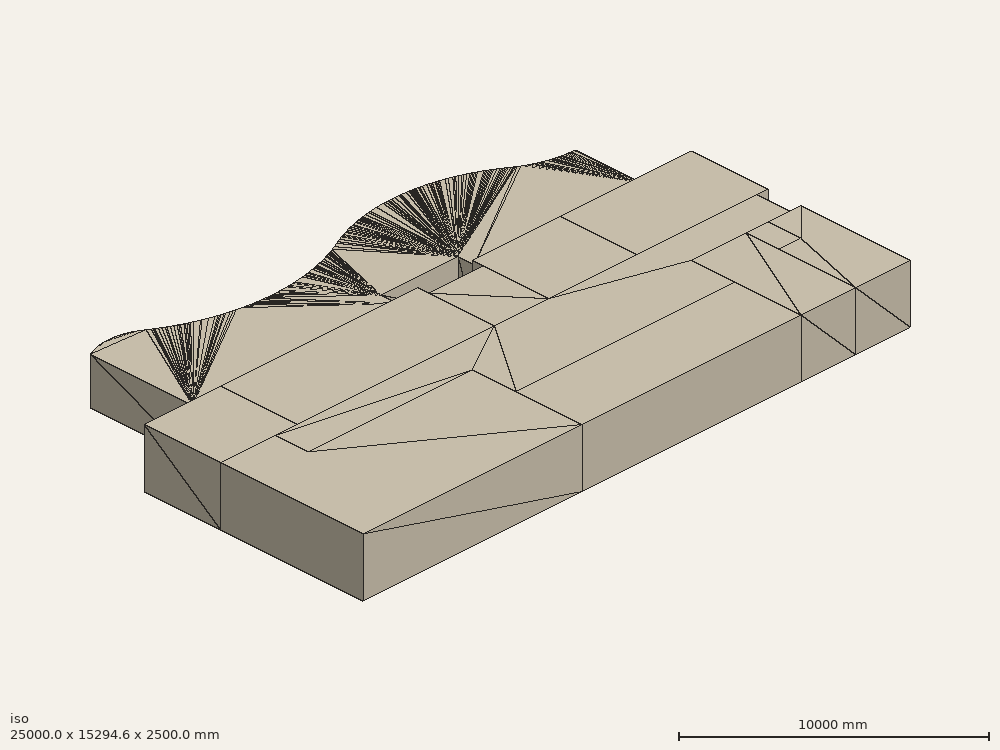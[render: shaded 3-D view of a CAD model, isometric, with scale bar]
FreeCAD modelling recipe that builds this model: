
FCSTD DOCUMENT  (FreeCAD 0.19R16466 (Git))
Label: Rooms_07
License: All rights reserved
LicenseURL: http://en.wikipedia.org/wiki/All_rights_reserved
objects: Part::FeaturePython×23, Part::Part2DObjectPython×10, App::GeometryPython×2, Sketcher::SketchObject×1
note: 36 computed .brp shape members not serialized (recipe doc carries the construction recipe); baked Part::Feature solids carry a one-line shape summary decoded from their .brp

FEATURE [Part::Part2DObjectPython] Wire  # Draft 2D object (typed FeaturePython)
  ChamferSize = 0
  Closed = true
  End = (0,6500,0)
  FilletRadius = 0
  Length = 33000
  MakeFace = true
  Points = (6) [(0,0,0),(10000,0,0),(10000,5000,0),(2500,5000,0),(2500,6500,0),(0,6500,0)]
  Start = (0,0,0)
  Subdivisions = 0
FEATURE [Part::Part2DObjectPython] Rectangle  # Draft 2D object (typed FeaturePython)
  ChamferSize = 0
  Columns = 1
  FilletRadius = 0
  Height = 3000
  Length = 10000
  MakeFace = true
  Placement = pos=(10000,0,0) rot=(0,0,1;0rad)
  Rows = 1
FEATURE [Part::Part2DObjectPython] Rectangle001  # Draft 2D object (typed FeaturePython)
  ChamferSize = 0
  Columns = 1
  FilletRadius = 0
  Height = 5000
  Length = 2500
  MakeFace = true
  Placement = pos=(20000,0,0) rot=(0,0,1;0rad)
  Rows = 1
FEATURE [Part::Part2DObjectPython] Wire001  # Draft 2D object (typed FeaturePython)
  ChamferSize = 0
  Closed = true
  End = (22500,3500,0)
  FilletRadius = 0
  Length = 15000
  MakeFace = true
  Points = (6) [(22500,0,0),(25000,0,0),(25000,5000,0),(23500,5000,0),(23500,3500,0),(22500,3500,0)]
  Start = (22500,0,0)
  Subdivisions = 0
FEATURE [Part::Part2DObjectPython] Rectangle002  # Draft 2D object (typed FeaturePython)
  ChamferSize = 0
  Columns = 1
  FilletRadius = 0
  Height = 1500
  Length = 1000
  MakeFace = true
  Placement = pos=(22500,3500,0) rot=(0,0,1;0rad)
  Rows = 1
FEATURE [Part::Part2DObjectPython] Rectangle003  # Draft 2D object (typed FeaturePython)
  ChamferSize = 0
  Columns = 1
  FilletRadius = 0
  Height = 3500
  Length = 3500
  MakeFace = true
  Placement = pos=(0,6500,0) rot=(0,0,1;0rad)
  Rows = 1
FEATURE [Part::Part2DObjectPython] Rectangle004  # Draft 2D object (typed FeaturePython)
  ChamferSize = 0
  Columns = 1
  FilletRadius = 0
  Height = 3500
  Length = 9000
  MakeFace = true
  Placement = pos=(3500,6500,0) rot=(0,0,1;0rad)
  Rows = 1
FEATURE [Part::Part2DObjectPython] Rectangle005  # Draft 2D object (typed FeaturePython)
  ChamferSize = 0
  Columns = 1
  FilletRadius = 0
  Height = 3500
  Length = 4000
  MakeFace = true
  Placement = pos=(15000,6500,0) rot=(0,0,1;0rad)
  Rows = 1
FEATURE [Part::Part2DObjectPython] Rectangle006  # Draft 2D object (typed FeaturePython)
  ChamferSize = 0
  Columns = 1
  FilletRadius = 0
  Height = 3500
  Length = 6000
  MakeFace = true
  Placement = pos=(19000,6500,0) rot=(0,0,1;0rad)
  Rows = 1
FEATURE [Part::Part2DObjectPython] Wire002  # Draft 2D object (typed FeaturePython)
  ChamferSize = 0
  Closed = true
  End = (10000,5000,0)
  FilletRadius = 0
  Length = 57000
  MakeFace = true
  Points = (12) [(2500,5000,0),(2500,6500,0),(12500,6500,0),(12500,9500,0),(15000,9500,0),(15000,6500,0),(24500,6500,0),(24500,5000,0),(20000,5000,0),(20000,3000,0),(10000,3000,0),(10000,5000,0)]
  Start = (2500,5000,0)
  Subdivisions = 0
FEATURE [Part::FeaturePython] Structure001  # Arch/BIM 0 (typed FeaturePython)
  Base = -> Rectangle002
  FaceMaker = 0
  Height = 2500
  HorizontalArea = 1.5e+06
  IfcData = attributes={"PredefinedType": {"name": "PredefinedType", "type": "IfcBeamTypeEnum", "is_enum": true, "enum_values": ["BEAM", "JOIST... (+96 chars omitted)
  IfcType = 0
  Length = 0
  MoveBase = false
  MoveWithHost = true
  Nodes = (2) [(23000,4250,0),(23000,4250,2500)]
  NodesOffset = 0
  Normal = (0,0,1)
  PerimeterLength = 5000
  PredefinedType = 0
  VerticalArea = 12500000
  Width = 200
FEATURE [Part::FeaturePython] Structure002  # Arch/BIM 0 (typed FeaturePython)
  Base = -> Rectangle001
  FaceMaker = 0
  Height = 2500
  HorizontalArea = 12500000
  IfcData = attributes={"PredefinedType": {"name": "PredefinedType", "type": "IfcBeamTypeEnum", "is_enum": true, "enum_values": ["BEAM", "JOIST... (+96 chars omitted)
  IfcType = 0
  Length = 0
  MoveBase = false
  MoveWithHost = true
  Nodes = (2) [(21250,2500,0),(21250,2500,2500)]
  NodesOffset = 0
  Normal = (0,0,1)
  PerimeterLength = 15000
  PredefinedType = 0
  VerticalArea = 37500000
  Width = 200
FEATURE [Part::FeaturePython] Structure003  # Arch/BIM 0 (typed FeaturePython)
  Base = -> Rectangle
  FaceMaker = 0
  Height = 2500
  HorizontalArea = 30000000
  IfcData = attributes={"PredefinedType": {"name": "PredefinedType", "type": "IfcBeamTypeEnum", "is_enum": true, "enum_values": ["BEAM", "JOIST... (+96 chars omitted)
  IfcType = 0
  Length = 0
  MoveBase = false
  MoveWithHost = true
  Nodes = (2) [(15000,1500,0),(15000,1500,2500)]
  NodesOffset = 0
  Normal = (0,0,1)
  PerimeterLength = 26000
  PredefinedType = 0
  VerticalArea = 65000000
  Width = 200
FEATURE [Part::FeaturePython] Structure004  # Arch/BIM 0 (typed FeaturePython)
  Base = -> Wire001
  FaceMaker = 0
  Height = 2500
  HorizontalArea = 11000000
  IfcData = attributes={"PredefinedType": {"name": "PredefinedType", "type": "IfcBeamTypeEnum", "is_enum": true, "enum_values": ["BEAM", "JOIST... (+96 chars omitted)
  IfcType = 0
  Length = 0
  MoveBase = false
  MoveWithHost = true
  Nodes = (2) [(23852.3,2261.36,0),(23852.3,2261.36,2500)]
  NodesOffset = 0
  Normal = (0,0,1)
  PerimeterLength = 15000
  PredefinedType = 0
  VerticalArea = 37500000
  Width = 200
FEATURE [Part::FeaturePython] Structure005  # Arch/BIM 0 (typed FeaturePython)
  Base = -> Rectangle005
  FaceMaker = 0
  Height = 2500
  HorizontalArea = 1.4e+07
  IfcData = attributes={"PredefinedType": {"name": "PredefinedType", "type": "IfcBeamTypeEnum", "is_enum": true, "enum_values": ["BEAM", "JOIST... (+96 chars omitted)
  IfcType = 0
  Length = 0
  MoveBase = false
  MoveWithHost = true
  Nodes = (2) [(17000,8250,0),(17000,8250,2500)]
  NodesOffset = 0
  Normal = (0,0,1)
  PerimeterLength = 15000
  PredefinedType = 0
  VerticalArea = 3.75e+07
  Width = 200
FEATURE [Part::FeaturePython] Structure006  # Arch/BIM 0 (typed FeaturePython)
  Base = -> Rectangle004
  FaceMaker = 0
  Height = 2500
  HorizontalArea = 31500000
  IfcData = attributes={"PredefinedType": {"name": "PredefinedType", "type": "IfcBeamTypeEnum", "is_enum": true, "enum_values": ["BEAM", "JOIST... (+96 chars omitted)
  IfcType = 0
  Length = 0
  MoveBase = false
  MoveWithHost = true
  Nodes = (2) [(8000,8250,0),(8000,8250,2500)]
  NodesOffset = 0
  Normal = (0,0,1)
  PerimeterLength = 25000
  PredefinedType = 0
  VerticalArea = 62500000
  Width = 200
FEATURE [Part::FeaturePython] Structure007  # Arch/BIM 0 (typed FeaturePython)
  Base = -> Rectangle003
  FaceMaker = 0
  Height = 2500
  HorizontalArea = 1.225e+07
  IfcData = attributes={"PredefinedType": {"name": "PredefinedType", "type": "IfcBeamTypeEnum", "is_enum": true, "enum_values": ["BEAM", "JOIST... (+96 chars omitted)
  IfcType = 0
  Length = 0
  MoveBase = false
  MoveWithHost = true
  Nodes = (2) [(1750,8250,0),(1750,8250,2500)]
  NodesOffset = 0
  Normal = (0,0,1)
  PerimeterLength = 14000
  PredefinedType = 0
  VerticalArea = 3.5e+07
  Width = 200
FEATURE [Part::FeaturePython] Structure008  # Arch/BIM 0 (typed FeaturePython)
  Base = -> Rectangle006
  FaceMaker = 0
  Height = 2500
  HorizontalArea = 21000000
  IfcData = attributes={"PredefinedType": {"name": "PredefinedType", "type": "IfcBeamTypeEnum", "is_enum": true, "enum_values": ["BEAM", "JOIST... (+96 chars omitted)
  IfcType = 0
  Length = 0
  MoveBase = false
  MoveWithHost = true
  Nodes = (2) [(22000,8250,0),(22000,8250,2500)]
  NodesOffset = 0
  Normal = (0,0,1)
  PerimeterLength = 19000
  PredefinedType = 0
  VerticalArea = 47500000
  Width = 200
FEATURE [Part::FeaturePython] Structure009  # Arch/BIM 0 (typed FeaturePython)
  Base = -> Wire002
  FaceMaker = 0
  Height = 2500
  HorizontalArea = 60500000
  IfcData = attributes={"PredefinedType": {"name": "PredefinedType", "type": "IfcBeamTypeEnum", "is_enum": true, "enum_values": ["BEAM", "JOIST... (+96 chars omitted)
  IfcType = 0
  Length = 0
  MoveBase = false
  MoveWithHost = true
  Nodes = (2) [(14026.9,5450.41,0),(14026.9,5450.41,2500)]
  NodesOffset = 0
  Normal = (0,0,1)
  PerimeterLength = 57000
  PredefinedType = 0
  VerticalArea = 142500000
  Width = 200
FEATURE [Part::FeaturePython] Space001  label="Restrooms"  # Arch/BIM 114 (typed FeaturePython)
  Area = 1.5e+06
  AutoPower = false
  Base = -> Structure001
  CompositionType = 0
  Conditioning = 0
  ElevationWithFlooring = 0
  EquipmentPower = 0
  FloorThickness = 0
  HorizontalArea = 0
  IfcData = IfcUID=0R3JkcNMSHwRku093rt3ko,+1 more (map truncated)
  IfcType = 114
  Internal = true
  LightingPower = 0
  MoveBase = false
  MoveWithHost = true
  NumberOfPeople = 0
  PerimeterLength = 5000
  PredefinedType = 3
  SpaceType = 0
  VerticalArea = 12500000
FEATURE [Part::FeaturePython] Space002  label="Left office"  # Arch/BIM 114 (typed FeaturePython)
  Area = 12500000
  AutoPower = false
  Base = -> Structure002
  CompositionType = 0
  Conditioning = 0
  ElevationWithFlooring = 0
  EquipmentPower = 0
  FloorThickness = 0
  HorizontalArea = 0
  IfcData = IfcUID=0R3du8NMSHwRku093rt3ko,+1 more (map truncated)
  IfcType = 114
  Internal = true
  LightingPower = 0
  MoveBase = false
  MoveWithHost = true
  NumberOfPeople = 0
  PerimeterLength = 15000
  PredefinedType = 3
  SpaceType = 0
  VerticalArea = 37500000
FEATURE [Part::FeaturePython] Space003  label="Lounge"  # Arch/BIM 114 (typed FeaturePython)
  Area = 30000000
  AutoPower = false
  Base = -> Structure003
  CompositionType = 0
  Conditioning = 0
  ElevationWithFlooring = 0
  EquipmentPower = 0
  FloorThickness = 0
  HorizontalArea = 0
  IfcData = IfcUID=0R3xAqNMSHwRku093rt3ko,+1 more (map truncated)
  IfcType = 114
  Internal = true
  LightingPower = 0
  MoveBase = false
  MoveWithHost = true
  NumberOfPeople = 0
  PerimeterLength = 26000
  PredefinedType = 3
  SpaceType = 0
  VerticalArea = 65000000
FEATURE [Part::FeaturePython] Space004  label="Right office"  # Arch/BIM 114 (typed FeaturePython)
  Area = 11000000
  AutoPower = false
  Base = -> Structure004
  CompositionType = 0
  Conditioning = 0
  ElevationWithFlooring = 0
  EquipmentPower = 0
  FloorThickness = 0
  HorizontalArea = 0
  IfcData = IfcUID=0R4E4qNMSHwRku093rt3ko,+1 more (map truncated)
  IfcType = 114
  Internal = true
  LightingPower = 0
  MoveBase = false
  MoveWithHost = true
  NumberOfPeople = 0
  PerimeterLength = 15000
  PredefinedType = 3
  SpaceType = 0
  VerticalArea = 37500000
FEATURE [Part::FeaturePython] Space005  label="Aux office"  # Arch/BIM 114 (typed FeaturePython)
  Area = 1.4e+07
  AutoPower = false
  Base = -> Structure005
  CompositionType = 0
  Conditioning = 0
  ElevationWithFlooring = 0
  EquipmentPower = 0
  FloorThickness = 0
  HorizontalArea = 0
  IfcData = IfcUID=0R4azMNMSHwRku093rt3ko,+1 more (map truncated)
  IfcType = 114
  Internal = true
  LightingPower = 0
  MoveBase = false
  MoveWithHost = true
  NumberOfPeople = 0
  PerimeterLength = 15000
  PredefinedType = 3
  SpaceType = 0
  VerticalArea = 3.75e+07
FEATURE [Part::FeaturePython] Space006  label="Large office"  # Arch/BIM 114 (typed FeaturePython)
  Area = 31500000
  AutoPower = false
  Base = -> Structure006
  CompositionType = 0
  Conditioning = 0
  ElevationWithFlooring = 0
  EquipmentPower = 0
  FloorThickness = 0
  HorizontalArea = 0
  IfcData = IfcUID=0R4tb4NMSHwRku093rt3ko,+1 more (map truncated)
  IfcType = 114
  Internal = true
  LightingPower = 0
  MoveBase = false
  MoveWithHost = true
  NumberOfPeople = 0
  PerimeterLength = 25000
  PredefinedType = 3
  SpaceType = 0
  VerticalArea = 62500000
FEATURE [Part::FeaturePython] Space007  label="Corner office"  # Arch/BIM 114 (typed FeaturePython)
  Area = 1.225e+07
  AutoPower = false
  Base = -> Structure007
  CompositionType = 0
  Conditioning = 0
  ElevationWithFlooring = 0
  EquipmentPower = 0
  FloorThickness = 0
  HorizontalArea = 0
  IfcData = IfcUID=0R5AIkNMSHwRku093rt3ko,+1 more (map truncated)
  IfcType = 114
  Internal = true
  LightingPower = 0
  MoveBase = false
  MoveWithHost = true
  NumberOfPeople = 0
  PerimeterLength = 14000
  PredefinedType = 3
  SpaceType = 0
  VerticalArea = 3.5e+07
FEATURE [Part::FeaturePython] Space008  label="Reception"  # Arch/BIM 114 (typed FeaturePython)
  Area = 21000000
  AutoPower = false
  Base = -> Structure008
  CompositionType = 0
  Conditioning = 0
  ElevationWithFlooring = 0
  EquipmentPower = 0
  FloorThickness = 0
  HorizontalArea = 0
  IfcData = IfcUID=0R5SGuNMSHwRku093rt3ko,+1 more (map truncated)
  IfcType = 114
  Internal = true
  LightingPower = 0
  MoveBase = false
  MoveWithHost = true
  NumberOfPeople = 0
  PerimeterLength = 19000
  PredefinedType = 3
  SpaceType = 0
  VerticalArea = 47500000
FEATURE [Part::FeaturePython] Space009  label="Circulation"  # Arch/BIM 114 (typed FeaturePython)
  Area = 60500000
  AutoPower = false
  Base = -> Structure009
  CompositionType = 0
  Conditioning = 0
  ElevationWithFlooring = 0
  EquipmentPower = 0
  FloorThickness = 0
  HorizontalArea = 0
  IfcData = IfcUID=0R5kPWNMSHwRku093rt3ko,+1 more (map truncated)
  IfcType = 114
  Internal = true
  LightingPower = 0
  MoveBase = false
  MoveWithHost = true
  NumberOfPeople = 0
  PerimeterLength = 57000
  PredefinedType = 3
  SpaceType = 0
  VerticalArea = 142500000
FEATURE [Sketcher::SketchObject] Sketch
  sketch-geometry (11):
    g0: LineSegment StartX=2593.64 StartY=10365 StartZ=0 EndX=11931.4 EndY=10365 EndZ=0
    g1: LineSegment StartX=11931.4 StartY=10365 StartZ=0 EndX=11931.4 EndY=11118 EndZ=0
    g2: LineSegment StartX=11931.4 StartY=11118 StartZ=0 EndX=15453.3 EndY=11118 EndZ=0
    g3: LineSegment StartX=15453.3 StartY=11118 StartZ=0 EndX=15453.3 EndY=10365 EndZ=0
    g4: LineSegment StartX=15453.3 StartY=10365 StartZ=0 EndX=23007 EndY=10365 EndZ=0
    g5: LineSegment StartX=23007 StartY=10365 StartZ=0 EndX=23007 EndY=13304.8 EndZ=0
    g6: ArcOfCircle CenterX=23007 CenterY=17437.3 CenterZ=0 NormalX=0 NormalY=0 NormalZ=1 AngleXU=0 Radius=4132.48 StartAngle=4.12392 EndAngle=4.71239
    g7: ArcOfCircle CenterX=16583.7 CenterY=7812.2 CenterZ=0 NormalX=0 NormalY=0 NormalZ=1 AngleXU=0 Radius=7439.05 StartAngle=0.982326 EndAngle=2.0282
    g8: ArcOfCircle CenterX=9509.7 CenterY=22183.8 CenterZ=0 NormalX=0 NormalY=0 NormalZ=1 AngleXU=0 Radius=8579.17 StartAngle=4.14982 EndAngle=5.1698
    g9: ArcOfCircle CenterX=3660.95 CenterY=12908 CenterZ=0 NormalX=0 NormalY=0 NormalZ=1 AngleXU=0 Radius=2386.59 StartAngle=1.00822 EndAngle=2.03444
    g10: LineSegment StartX=2593.64 StartY=15042.6 StartZ=0 EndX=2593.64 EndY=10365 EndZ=0
  constraints (19):
    c: Horizontal(g0)
    c: Coincident(g0,g1)
    c: Vertical(g1)
    c: Coincident(g1,g2)
    c: Horizontal(g2)
    c: Coincident(g2,g3)
    c: Coincident(g3,g4)
    c: Horizontal(g4)
    c: Coincident(g4,g5)
    c: Vertical(g5)
    c: Perpendicular(g5,g6) = 4.71239
    c: Tangent(g6,g7) = 1.5708
    c: Tangent(g7,g8) = 1.5708
    c: Tangent(g8,g9) = 1.5708
    c: Coincident(g9,g10)
    c: Coincident(g10,g0)
    c: Vertical(g10)
    c: Vertical(g3)
    c: Equal(g1,g3)
FEATURE [Part::FeaturePython] Structure010  # Arch/BIM 0 (typed FeaturePython)
  Base = -> Sketch
  FaceMaker = 0
  Height = 2000
  HorizontalArea = 7.979e+07
  IfcData = attributes={"PredefinedType": {"name": "PredefinedType", "type": "IfcBeamTypeEnum", "is_enum": true, "enum_values": ["BEAM", "JOIST... (+96 chars omitted)
  IfcType = 0
  Length = 0
  MoveBase = false
  MoveWithHost = true
  Nodes = (2) [(12641.3,12493,0),(12641.3,12493,2000)]
  NodesOffset = 0
  Normal = (0,0,0)
  PerimeterLength = 50948.8
  PredefinedType = 0
  VerticalArea = 1.01898e+08
  Width = 200
FEATURE [Part::FeaturePython] Space010  label="Garden"  # Arch/BIM 114 (typed FeaturePython)
  Area = 7.979e+07
  AutoPower = false
  Base = -> Structure010
  CompositionType = 0
  Conditioning = 0
  ElevationWithFlooring = 0
  EquipmentPower = 0
  FloorThickness = 0
  HorizontalArea = 0
  IfcData = IfcUID=0R6K3CNMSHwRku093rt3ko,+1 more (map truncated)
  IfcType = 114
  Internal = true
  LightingPower = 0
  MoveBase = false
  MoveWithHost = true
  NumberOfPeople = 0
  PerimeterLength = 50948.8
  PredefinedType = 4
  SpaceType = 0
  VerticalArea = 1.01898e+08
FEATURE [Part::FeaturePython] Structure  # Arch/BIM 0 (typed FeaturePython)
  Base = -> Wire
  FaceMaker = 0
  Height = 2500
  HorizontalArea = 53750000
  IfcData = attributes={"PredefinedType": {"name": "PredefinedType", "type": "IfcBeamTypeEnum", "is_enum": true, "enum_values": ["BEAM", "JOIST... (+96 chars omitted)
  IfcType = 0
  Length = 0
  MoveBase = false
  MoveWithHost = true
  Nodes = (2) [(4738.37,2726.74,0),(4738.37,2726.74,2500)]
  NodesOffset = 0
  Normal = (0,0,1)
  PerimeterLength = 33000
  PredefinedType = 0
  VerticalArea = 82500000
  Width = 200
FEATURE [Part::FeaturePython] Space  label="Meeting room"  # Arch/BIM 114 (typed FeaturePython)
  Area = 53750000
  AutoPower = false
  Base = -> Structure
  CompositionType = 0
  Conditioning = 0
  ElevationWithFlooring = 0
  EquipmentPower = 0
  FloorThickness = 0
  HorizontalArea = 0
  IfcData = IfcUID=0R2g0wNMSHwRku093rt3ko,+1 more (map truncated)
  IfcType = 114
  Internal = true
  LightingPower = 0
  MoveBase = false
  MoveWithHost = true
  NumberOfPeople = 0
  PerimeterLength = 33000
  PredefinedType = 3
  SpaceType = 0
  VerticalArea = 82500000
FEATURE [App::GeometryPython] BuildingPart  label="Ground Floor"  # Arch/BIM 14 (typed FeaturePython)
  Area = 0
  CompositionType = 0
  Elevation = 0
  Group = -> [Space,Space001,Space002,Space003,Space004,Space005,Space006,Space007,Space008,Space009,Space010]
  Height = 0
  IfcData = IfcUID=0R2Q26NMSHwRku093rt3ko,+1 more (map truncated)
  IfcType = 14
  LevelOffset = 0
FEATURE [App::GeometryPython] BuildingPart001  label="Office Building"  # Arch/BIM 11 (typed FeaturePython)
  Area = 0
  BuildingType = 0
  CompositionType = 0
  ElevationOfRefHeight = 0
  ElevationOfTerrain = 0
  Group = -> [BuildingPart]
  Height = 0
  IfcData = IfcUID=0R1$3ONMSHwRku093rt3ko,+1 more (map truncated)
  IfcType = 11
  LevelOffset = 0
FEATURE [Part::FeaturePython] Site  label="Somewhere"  # Arch/BIM 109 (typed FeaturePython)
  AdditionVolume = 0
  Area = 3.2779e+08
  CompositionType = 0
  Declination = 0
  Elevation = 0
  ExtrusionVector = (0,0,-100000)
  Group = -> [BuildingPart001]
  Height = 0
  IfcData = IfcUID=0R0qxANMSHwRku093rt3ko,+1 more (map truncated)
  IfcType = 109
  Latitude = 0
  Longitude = 0
  OriginOffset = (0,0,0)
  Perimeter = 0
  ProjectedArea = 0
  RefElevation = 0
  RemoveSplitter = false
  SubtractionVolume = 0
